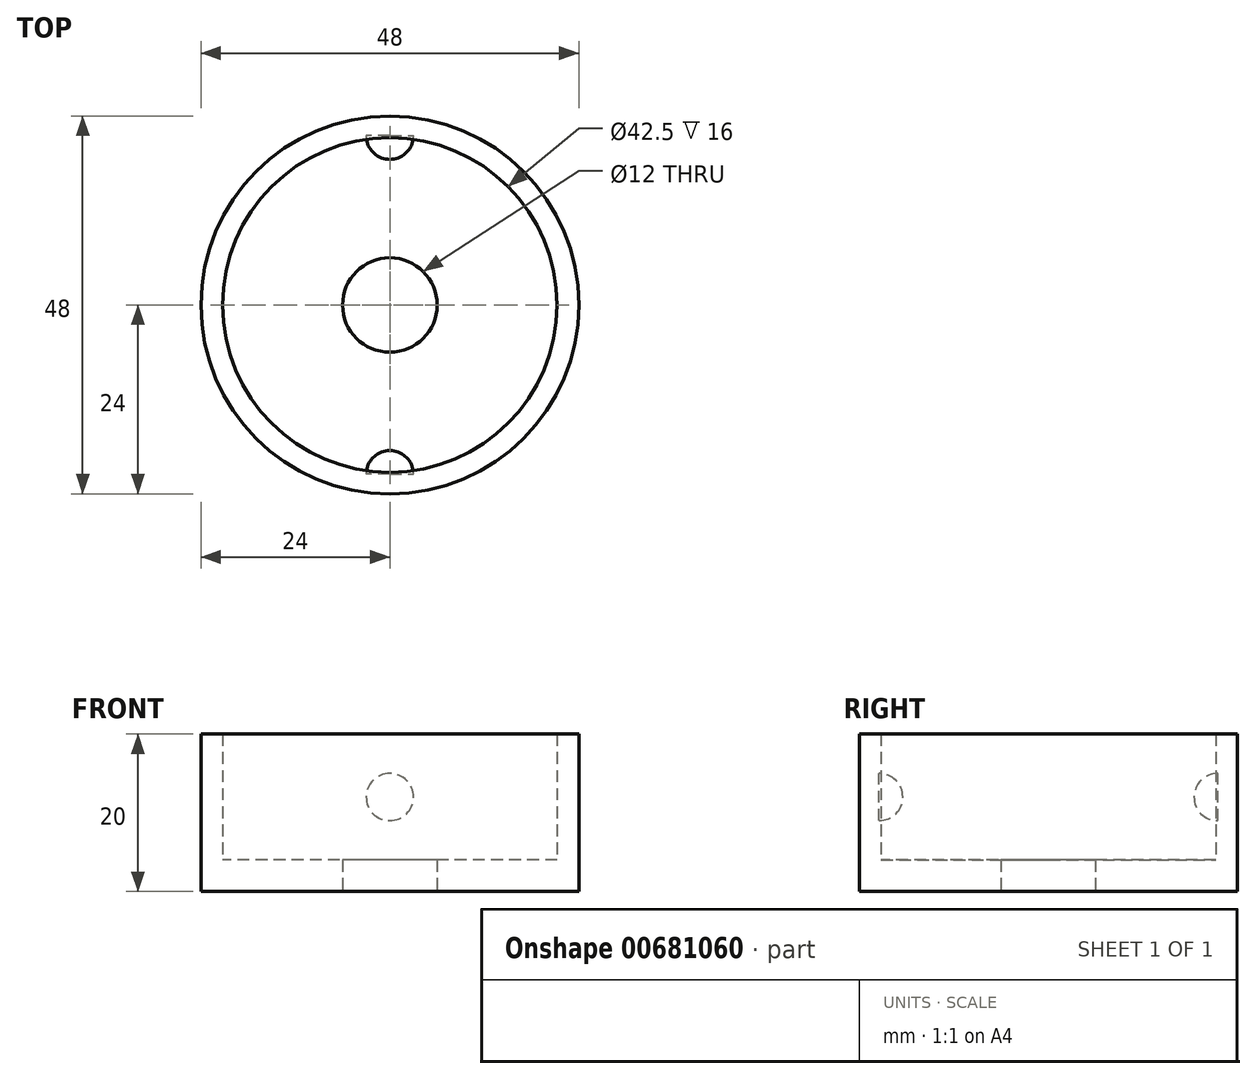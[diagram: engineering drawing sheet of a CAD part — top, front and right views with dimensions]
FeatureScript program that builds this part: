
annotation { "Feature Type Name" : "Feature", "Feature Type Description" : "" }
export const myFeature = defineFeature(function(context is Context, id is Id, definition is map)
    precondition{}
    {
        {
            var Q0;
            Q0=qCreatedBy(makeId("Top.planeOp"),FACE);
            var sketch = newSketch(context, id + "F0", { "sketchPlane" : qUnion([Q0])});
            skCircle(sketch, "E0", {"center": v(0, 0) * mm, "radius": 21.25 * mm});
            skCircle(sketch, "E1", {"center": v(0, 0) * mm, "radius": 24 * mm});
            skSolve(sketch);
        }
        {
            var Q0;
            Q0=qSketchRegion(id+"F0",true);
            extrude(context, id + "F1", {"entities" : qUnion([Q0]), "depth" : 20 * mm, "offsetDistance" : 25 * mm});
        }
        {
            var Q0;
            Q0=qCreatedBy(makeId("Top.planeOp"),FACE);
            var sketch = newSketch(context, id + "F2", { "sketchPlane" : qUnion([Q0])});
            skCircle(sketch, "E2", {"center": v(0, 0) * mm, "radius": 24 * mm});
            skSolve(sketch);
        }
        {
            var Q0;
            Q0 = qSketchRegion(id + "F2", true);
            extrude(context, id + "F3", {"entities" : qUnion([Q0]), "operationType" : NewBodyOperationType.ADD, "depth" : 4 * mm, "offsetDistance" : 25 * mm});
        }
        {
            var Q0;
            Q0=qCreatedBy(makeId("Front.planeOp"),FACE);
            var sketch = newSketch(context, id + "F4", { "sketchPlane" : qUnion([Q0])});
            skLineSegment(sketch, "E3", {"start": v(0, 0) * mm, "end": v(0, 12) * mm});
            skArc(sketch, "E4", {"start": v(0, 9) * mm, "mid": v(3, 12) * mm, "end": v(0, 15) * mm});
            skLineSegment(sketch, "E5", {"start": v(0, 12) * mm, "end": v(0, 15) * mm});
            skSolve(sketch);
        }
        {
            var Q0;
            {var subQ2=sQuery(id+"F4.wireOp",EDGE,"E4");Q0=makeQuery(id+"F4.imprint","IMPRINT",FACE,{"disambiguationData":[TD([[makeQuery(id+"F4.imprint","IMPRINT",EDGE,{"derivedFrom":subQ2}),1.0]])]});}
            var Q1;
            Q1=sQuery(id+"F4.wireOp",EDGE,"E3");
            revolve(context, id + "F5", {"surfaceOperationType" : NewSurfaceOperationType.NEW, "entities" : qUnion([Q0]), "axis" : qUnion([Q1]), "revolveType" : RevolveType.ONE_DIRECTION, "angle" : 180 * degree});
        }
        {
            var Q0;
            Q0=makeQuery(id+"F5.opRevolve","SWEPT_BODY",BODY,{"disambiguationData":[OSD([sQuery(id+"F4.wireOp",EDGE,"E3"),sQuery(id+"F4.wireOp",EDGE,"E4"),sQuery(id+"F4.wireOp",EDGE,"E5")])]});
            transform(context, id + "F6", {"entities" : qUnion([Q0]), "transformType" : TransformType.TRANSLATION_3D, "dx" : 0 * mm, "dy" : -21.5 * mm, "dz" : 0 * mm, "makeCopy" : true});
        }
        {
            var Q0;
            Q0=qCreatedBy(makeId("Right.planeOp"),FACE);
            var sketch = newSketch(context, id + "F7", { "sketchPlane" : qUnion([Q0])});
            skLineSegment(sketch, "E6", {"start": v(0, 0) * mm, "end": v(0, 10) * mm});
            skSolve(sketch);
        }
        {
            var Q0;
            Q0=makeQuery(id+"F5.opRevolve","SWEPT_BODY",BODY,{"disambiguationData":[OSD([sQuery(id+"F4.wireOp",EDGE,"E3"),sQuery(id+"F4.wireOp",EDGE,"E4"),sQuery(id+"F4.wireOp",EDGE,"E5")])]});
            var Q1;
            Q1=sQuery(id+"F7.wireOp",EDGE,"E6");
            transform(context, id + "F8", {"entities" : qUnion([Q0]), "transformType" : TransformType.ROTATION, "transformAxis" : qUnion([Q1]), "angle" : 180 * degree, "makeCopy" : false});
        }
        {
            var Q0;
            Q0=makeQuery(id+"F5.opRevolve","SWEPT_BODY",BODY,{"disambiguationData":[OSD([sQuery(id+"F4.wireOp",EDGE,"E3"),sQuery(id+"F4.wireOp",EDGE,"E4"),sQuery(id+"F4.wireOp",EDGE,"E5")])]});
            transform(context, id + "F9", {"entities" : qUnion([Q0]), "transformType" : TransformType.TRANSLATION_3D, "dx" : 0 * mm, "dy" : 21.5 * mm, "dz" : 0 * mm, "makeCopy" : false});
        }
        {
            var Q0;
            Q0=qCreatedBy(makeId("Top.planeOp"),FACE);
            var sketch = newSketch(context, id + "F10", { "sketchPlane" : qUnion([Q0])});
            skCircle(sketch, "E7", {"center": v(0, 0) * mm, "radius": 6 * mm});
            skSolve(sketch);
        }
        {
            var Q0;
            Q0 = qSketchRegion(id + "F10", true);
            extrude(context, id + "F11", {"entities" : qUnion([Q0]), "depth" : 5 * mm, "offsetDistance" : 25 * mm});
        }
        {
            var Q0;
            Q0=makeQuery(id+"F11.opExtrude","SWEPT_BODY",BODY,{"disambiguationData":[OSD([sQuery(id+"F10.wireOp",EDGE,"E7")])]});
            var Q1;
            Q1=makeQuery(id+"F1.opExtrude","SWEPT_BODY",BODY,{"disambiguationData":[OSD([sQuery(id+"F0.wireOp",EDGE,"E0"),sQuery(id+"F0.wireOp",EDGE,"E1")])]});
            booleanBodies(context, id + "F12", {"operationType" : BooleanOperationType.SUBTRACTION, "tools" : qUnion([Q0]), "targets" : qUnion([Q1])});
        }
    });
